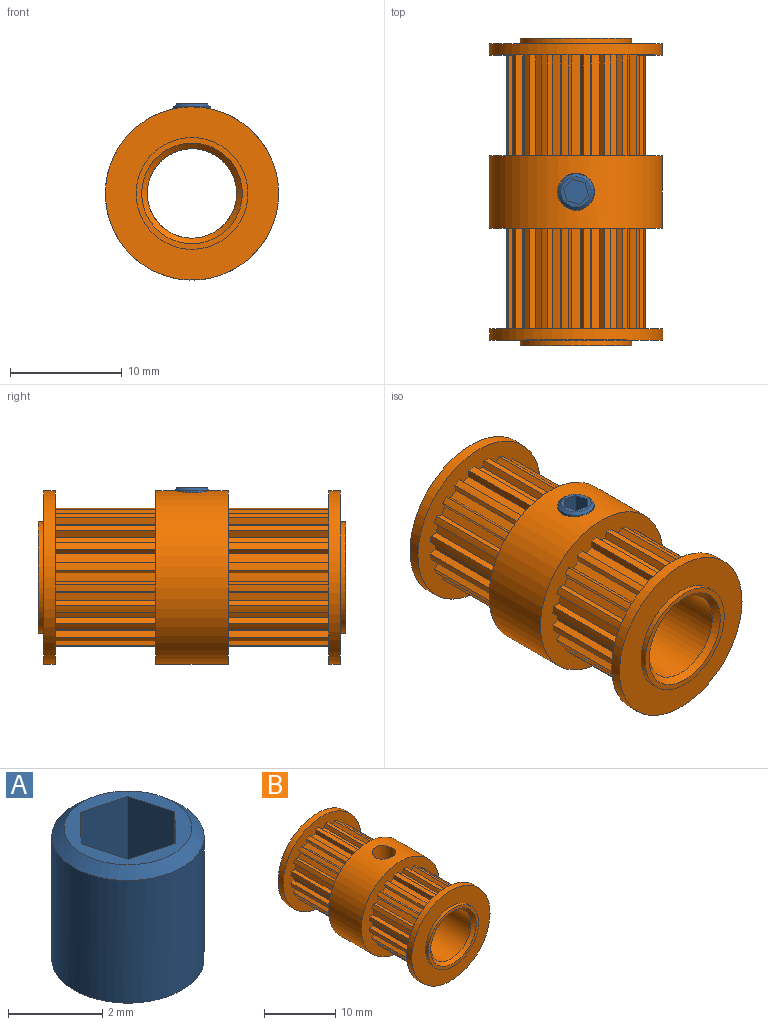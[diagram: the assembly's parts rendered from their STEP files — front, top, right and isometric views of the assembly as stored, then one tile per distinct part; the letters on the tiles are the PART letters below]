
ASSEMBLY  parts=2 mates=1
PART A: 12 faces, bbox 3.2x3.2x4 mm
  f0: plane 3x1.12mm, normal (0.25,0.97,0), area 3.5mm2, adj f1,f2,f4,f7
  f1: plane 3x1.11mm, normal (0.96,0.27,0), area 3.5mm2, adj f0,f3,f4,f7
  f2: plane 3x0.83mm, normal (-0.72,0.7,0), area 3.5mm2, adj f0,f4,f5,f7
  f3: plane 3x0.83mm, normal (0.72,-0.7,0), area 3.5mm2, adj f1,f4,f6,f7
  f4: plane 2.24x2.22mm, normal (0,0,1), area 3.5mm2, adj f0,f1,f2,f3,f5,f6
  f5: plane 3x1.11mm, normal (-0.96,-0.27,0), area 3.5mm2, adj f2,f4,f6,f7
  f6: plane 3x1.12mm, normal (-0.25,-0.97,0), area 3.5mm2, adj f3,f4,f5,f7
  f7: plane 2.71x2.71mm, normal (0,0,1), area 2.3mm2, adj f0,f1,f2,f3,f5,f6,f9
  f8: plane 1.19x1.19mm, normal (0,0,-1), area 1.1mm2, adj f10
  f9: cone r=1.61mm half-angle=48.9deg, axis (0,0,-1), area 3.2mm2, adj f7,f11
  f10: cone r=1.61mm half-angle=59.8deg, axis (0,0,1), area 8.2mm2, adj f8,f11
  f11: cylinder r=1.61mm len=3.23mm, axis (0,0,-1), area 32.3mm2, adj f9,f10
PART B: 177 faces, bbox 15.5x27.5x15.5 mm
  f0: plane 9x0.64mm, normal (1,0,-0.08), area 5.8mm2, adj f2,f3,f155,f167
  f1: plane 9x0.76mm, normal (0.95,0,0.31), area 7.2mm2, adj f4,f5,f158,f168
  f2: plane 9x0.76mm, normal (0.31,0,-0.95), area 7.2mm2, adj f0,f6,f155,f167
  f3: cylinder r=6.21mm len=9mm, axis (0,1,0), area 5.9mm2, adj f0,f7,f155,f167
  f4: plane 9x0.64mm, normal (0.08,0,1), area 5.8mm2, adj f1,f8,f158,f168
  f5: plane 9x0.49mm, normal (0.65,0,-0.76), area 5.8mm2, adj f1,f9,f158,f168
  f6: plane 9x0.49mm, normal (-0.76,0,-0.65), area 5.8mm2, adj f2,f10,f155,f167
  f7: plane 9x0.59mm, normal (-0.92,0,-0.38), area 5.8mm2, adj f3,f11,f155,f167
  f8: cylinder r=6.21mm len=9mm, axis (0,-1,0), area 5.9mm2, adj f4,f12,f158,f168
  f9: cylinder r=6.21mm len=9mm, axis (0,-1,0), area 5.9mm2, adj f5,f13,f158,f168
  f10: cylinder r=6.21mm len=9mm, axis (0,1,0), area 5.9mm2, adj f6,f14,f155,f167
  f11: plane 9x0.8mm, normal (0,0,-1), area 7.2mm2, adj f7,f15,f155,f167
  f12: plane 9x0.59mm, normal (0.38,0,-0.92), area 5.8mm2, adj f8,f16,f158,f168
  f13: plane 9x0.63mm, normal (-0.23,0,0.97), area 5.8mm2, adj f9,f17,f158,f168
  f14: plane 9x0.63mm, normal (0.97,0,0.23), area 5.8mm2, adj f10,f18,f155,f167
  f15: plane 9x0.59mm, normal (0.92,0,-0.38), area 5.8mm2, adj f11,f19,f155,f167
  f16: plane 9x0.8mm, normal (1,0,0), area 7.2mm2, adj f12,f20,f158,f168
  f17: plane 9x0.65mm, normal (0.81,0,0.59), area 7.2mm2, adj f13,f21,f158,f168
  f18: plane 9x0.65mm, normal (0.59,0,-0.81), area 7.2mm2, adj f14,f22,f155,f167
  f19: cylinder r=6.21mm len=9mm, axis (0,1,0), area 5.9mm2, adj f15,f23,f155,f167
  f20: plane 9x0.59mm, normal (0.38,0,0.92), area 5.8mm2, adj f16,f24,f158,f168
  f21: plane 9x0.55mm, normal (0.85,0,-0.52), area 5.8mm2, adj f17,f25,f158,f168
  f22: plane 9x0.55mm, normal (-0.52,0,-0.85), area 5.8mm2, adj f18,f26,f155,f167
  f23: plane 9x0.64mm, normal (-1,0,-0.08), area 5.8mm2, adj f19,f27,f155,f167
  f24: cylinder r=6.21mm len=9mm, axis (0,-1,0), area 5.9mm2, adj f20,f28,f158,f168
  f25: cylinder r=6.21mm len=9mm, axis (0,-1,0), area 5.9mm2, adj f21,f29,f158,f168
  f26: cylinder r=6.21mm len=9mm, axis (0,1,0), area 5.9mm2, adj f22,f30,f155,f167
  f27: plane 9x0.76mm, normal (-0.31,0,-0.95), area 7.2mm2, adj f23,f31,f155,f167
  f28: plane 9x0.64mm, normal (0.08,0,-1), area 5.8mm2, adj f24,f32,f158,f168
  f29: plane 9x0.55mm, normal (-0.52,0,0.85), area 5.8mm2, adj f25,f33,f158,f168
  f30: plane 9x0.55mm, normal (0.85,0,0.52), area 5.8mm2, adj f26,f34,f155,f167
  f31: plane 9x0.49mm, normal (0.76,0,-0.65), area 5.8mm2, adj f27,f35,f155,f167
  f32: plane 9x0.76mm, normal (0.95,0,-0.31), area 7.2mm2, adj f28,f36,f158,f168
  f33: plane 9x0.65mm, normal (0.59,0,0.81), area 7.2mm2, adj f29,f37,f158,f168
  f34: plane 9x0.65mm, normal (0.81,0,-0.59), area 7.2mm2, adj f30,f38,f155,f167
  f35: cylinder r=6.21mm len=9mm, axis (0,1,0), area 5.9mm2, adj f31,f39,f155,f167
  f36: plane 9x0.49mm, normal (0.65,0,0.76), area 5.8mm2, adj f32,f40,f158,f168
  f37: plane 9x0.63mm, normal (0.97,0,-0.23), area 5.8mm2, adj f33,f41,f158,f168
  f38: plane 9x0.63mm, normal (-0.23,0,-0.97), area 5.8mm2, adj f34,f42,f155,f167
  f39: plane 9x0.63mm, normal (-0.97,0,0.23), area 5.8mm2, adj f35,f43,f155,f167
  f40: cylinder r=6.21mm len=9mm, axis (0,-1,0), area 5.9mm2, adj f36,f44,f158,f168
  f41: cylinder r=6.21mm len=9mm, axis (0,-1,0), area 5.9mm2, adj f37,f45,f158,f168
  f42: cylinder r=6.21mm len=9mm, axis (0,1,0), area 5.9mm2, adj f38,f46,f155,f167
  f43: plane 9x0.65mm, normal (-0.59,0,-0.81), area 7.2mm2, adj f39,f47,f155,f167
  f44: plane 9x0.63mm, normal (-0.23,0,-0.97), area 5.8mm2, adj f40,f48,f158,f168
  f45: plane 9x0.49mm, normal (-0.76,0,0.65), area 5.8mm2, adj f41,f49,f158,f168
  f46: plane 9x0.49mm, normal (0.65,0,0.76), area 5.8mm2, adj f42,f50,f155,f167
  f47: plane 9x0.55mm, normal (0.52,0,-0.85), area 5.8mm2, adj f43,f51,f155,f167
  f48: plane 9x0.65mm, normal (0.81,0,-0.59), area 7.2mm2, adj f44,f52,f158,f168
  f49: plane 9x0.76mm, normal (0.31,0,0.95), area 7.2mm2, adj f45,f53,f158,f168
  f50: plane 9x0.76mm, normal (0.95,0,-0.31), area 7.2mm2, adj f46,f54,f155,f167
  f51: cylinder r=6.21mm len=9mm, axis (0,1,0), area 5.9mm2, adj f47,f55,f155,f167
  f52: plane 9x0.55mm, normal (0.85,0,0.52), area 5.8mm2, adj f48,f56,f158,f168
  f53: plane 9x0.64mm, normal (1,0,0.08), area 5.8mm2, adj f49,f57,f158,f168
  f54: plane 9x0.64mm, normal (0.08,0,-1), area 5.8mm2, adj f50,f58,f155,f167
  f55: plane 9x0.55mm, normal (-0.85,0,0.52), area 5.8mm2, adj f51,f59,f155,f167
  f56: cylinder r=6.21mm len=9mm, axis (0,-1,0), area 5.9mm2, adj f52,f60,f158,f168
  f57: cylinder r=6.21mm len=9mm, axis (0,-1,0), area 5.9mm2, adj f53,f61,f158,f168
  f58: cylinder r=6.21mm len=9mm, axis (0,1,0), area 5.9mm2, adj f54,f62,f155,f167
  f59: plane 9x0.65mm, normal (-0.81,0,-0.59), area 7.2mm2, adj f55,f63,f155,f167
  f60: plane 9x0.55mm, normal (-0.52,0,-0.85), area 5.8mm2, adj f56,f64,f158,f168
  f61: plane 9x0.59mm, normal (-0.92,0,0.38), area 5.8mm2, adj f57,f65,f158,f168
  f62: plane 9x0.59mm, normal (0.38,0,0.92), area 5.8mm2, adj f58,f66,f155,f167
  f63: plane 9x0.63mm, normal (0.23,0,-0.97), area 5.8mm2, adj f59,f67,f155,f167
  f64: plane 9x0.65mm, normal (0.59,0,-0.81), area 7.2mm2, adj f60,f68,f158,f168
  f65: plane 9x0.8mm, normal (0,0,1), area 7.2mm2, adj f61,f69,f158,f168
  f66: plane 9x0.8mm, normal (1,0,0), area 7.2mm2, adj f62,f70,f155,f167
  f67: cylinder r=6.21mm len=9mm, axis (0,1,0), area 5.9mm2, adj f63,f71,f155,f167
  f68: plane 9x0.63mm, normal (0.97,0,0.23), area 5.8mm2, adj f64,f72,f158,f168
  f69: plane 9x0.59mm, normal (0.92,0,0.38), area 5.8mm2, adj f65,f73,f158,f168
  f70: plane 9x0.59mm, normal (0.38,0,-0.92), area 5.8mm2, adj f66,f74,f155,f167
  f71: plane 9x0.49mm, normal (-0.65,0,0.76), area 5.8mm2, adj f67,f75,f155,f167
  f72: cylinder r=6.21mm len=9mm, axis (0,-1,0), area 5.9mm2, adj f68,f76,f158,f168
  f73: cylinder r=6.21mm len=9mm, axis (0,-1,0), area 5.9mm2, adj f69,f77,f158,f168
  f74: cylinder r=6.21mm len=9mm, axis (0,1,0), area 5.9mm2, adj f70,f78,f155,f167
  f75: plane 9x0.76mm, normal (-0.95,0,-0.31), area 7.2mm2, adj f71,f79,f155,f167
  f76: plane 9x0.49mm, normal (-0.76,0,-0.65), area 5.8mm2, adj f72,f80,f158,f168
  f77: plane 9x0.64mm, normal (-1,0,0.08), area 5.8mm2, adj f73,f81,f158,f168
  f78: plane 9x0.64mm, normal (0.08,0,1), area 5.8mm2, adj f74,f82,f155,f167
  f79: plane 9x0.64mm, normal (-0.08,0,-1), area 5.8mm2, adj f75,f83,f155,f167
  f80: plane 9x0.76mm, normal (0.31,0,-0.95), area 7.2mm2, adj f76,f84,f158,f168
  f81: plane 9x0.76mm, normal (-0.31,0,0.95), area 7.2mm2, adj f77,f85,f158,f168
  f82: plane 9x0.76mm, normal (0.95,0,0.31), area 7.2mm2, adj f78,f86,f155,f167
  f83: cylinder r=6.21mm len=9mm, axis (0,1,0), area 5.9mm2, adj f79,f87,f155,f167
  f84: plane 9x0.64mm, normal (1,0,-0.08), area 5.8mm2, adj f80,f88,f158,f168
  f85: plane 9x0.49mm, normal (0.76,0,0.65), area 5.8mm2, adj f81,f89,f158,f168
  f86: plane 9x0.49mm, normal (0.65,0,-0.76), area 5.8mm2, adj f82,f90,f155,f167
  f87: plane 9x0.59mm, normal (-0.38,0,0.92), area 5.8mm2, adj f83,f91,f155,f167
  f88: cylinder r=6.21mm len=9mm, axis (0,-1,0), area 5.9mm2, adj f84,f92,f158,f168
  f89: cylinder r=6.21mm len=9mm, axis (0,-1,0), area 5.9mm2, adj f85,f93,f158,f168
  f90: cylinder r=6.21mm len=9mm, axis (0,1,0), area 5.9mm2, adj f86,f94,f155,f167
  f91: plane 9x0.8mm, normal (-1,0,0), area 7.2mm2, adj f87,f95,f155,f167
  f92: plane 9x0.59mm, normal (-0.92,0,-0.38), area 5.8mm2, adj f88,f96,f158,f168
  f93: plane 9x0.63mm, normal (-0.97,0,-0.23), area 5.8mm2, adj f89,f97,f158,f168
  f94: plane 9x0.63mm, normal (-0.23,0,0.97), area 5.8mm2, adj f90,f98,f155,f167
  f95: plane 9x0.59mm, normal (-0.38,0,-0.92), area 5.8mm2, adj f91,f99,f155,f167
  f96: plane 9x0.8mm, normal (0,0,-1), area 7.2mm2, adj f92,f100,f158,f168
  f97: plane 9x0.65mm, normal (-0.59,0,0.81), area 7.2mm2, adj f93,f101,f158,f168
  f98: plane 9x0.65mm, normal (0.81,0,0.59), area 7.2mm2, adj f94,f102,f155,f167
  f99: cylinder r=6.21mm len=9mm, axis (0,1,0), area 5.9mm2, adj f95,f103,f155,f167
  f100: plane 9x0.59mm, normal (0.92,0,-0.38), area 5.8mm2, adj f96,f104,f158,f168
  f101: plane 9x0.55mm, normal (0.52,0,0.85), area 5.8mm2, adj f97,f105,f158,f168
  f102: plane 9x0.55mm, normal (0.85,0,-0.52), area 5.8mm2, adj f98,f106,f155,f167
  f103: plane 9x0.64mm, normal (-0.08,0,1), area 5.8mm2, adj f99,f107,f155,f167
  f104: cylinder r=6.21mm len=9mm, axis (0,-1,0), area 5.9mm2, adj f100,f108,f158,f168
  f105: cylinder r=6.21mm len=9mm, axis (0,-1,0), area 5.9mm2, adj f101,f109,f158,f168
  f106: cylinder r=6.21mm len=9mm, axis (0,1,0), area 5.9mm2, adj f102,f110,f155,f167
  f107: plane 9x0.76mm, normal (-0.95,0,0.31), area 7.2mm2, adj f103,f111,f155,f167
  f108: plane 9x0.64mm, normal (-1,0,-0.08), area 5.8mm2, adj f104,f112,f158,f168
  f109: plane 9x0.55mm, normal (-0.85,0,-0.52), area 5.8mm2, adj f105,f113,f158,f168
  f110: plane 9x0.55mm, normal (-0.52,0,0.85), area 5.8mm2, adj f106,f114,f155,f167
  f111: plane 9x0.49mm, normal (-0.65,0,-0.76), area 5.8mm2, adj f107,f115,f155,f167
  f112: plane 9x0.76mm, normal (-0.31,0,-0.95), area 7.2mm2, adj f108,f116,f158,f168
  f113: plane 9x0.65mm, normal (-0.81,0,0.59), area 7.2mm2, adj f109,f117,f158,f168
  f114: plane 9x0.65mm, normal (0.59,0,0.81), area 7.2mm2, adj f110,f118,f155,f167
  f115: cylinder r=6.21mm len=9mm, axis (0,1,0), area 5.9mm2, adj f111,f119,f155,f167
  f116: plane 9x0.49mm, normal (0.76,0,-0.65), area 5.8mm2, adj f112,f120,f158,f168
  f117: plane 9x0.63mm, normal (0.23,0,0.97), area 5.8mm2, adj f113,f121,f158,f168
  f118: plane 9x0.63mm, normal (0.97,0,-0.23), area 5.8mm2, adj f114,f122,f155,f167
  f119: plane 9x0.63mm, normal (0.23,0,0.97), area 5.8mm2, adj f115,f123,f155,f167
  f120: cylinder r=6.21mm len=9mm, axis (0,-1,0), area 5.9mm2, adj f116,f124,f158,f168
  f121: cylinder r=6.21mm len=9mm, axis (0,-1,0), area 5.9mm2, adj f117,f125,f158,f168
  f122: cylinder r=6.21mm len=9mm, axis (0,1,0), area 5.9mm2, adj f118,f126,f155,f167
  f123: plane 9x0.65mm, normal (-0.81,0,0.59), area 7.2mm2, adj f119,f127,f155,f167
  f124: plane 9x0.63mm, normal (-0.97,0,0.23), area 5.8mm2, adj f120,f128,f158,f168
  f125: plane 9x0.49mm, normal (-0.65,0,-0.76), area 5.8mm2, adj f121,f129,f158,f168
  f126: plane 9x0.49mm, normal (-0.76,0,0.65), area 5.8mm2, adj f122,f130,f155,f167
  f127: plane 9x0.55mm, normal (-0.85,0,-0.52), area 5.8mm2, adj f123,f131,f155,f167
  f128: plane 9x0.65mm, normal (-0.59,0,-0.81), area 7.2mm2, adj f124,f132,f158,f168
  f129: plane 9x0.76mm, normal (-0.95,0,0.31), area 7.2mm2, adj f125,f133,f158,f168
  f130: plane 9x0.76mm, normal (0.31,0,0.95), area 7.2mm2, adj f126,f134,f155,f167
  f131: cylinder r=6.21mm len=9mm, axis (0,1,0), area 5.9mm2, adj f127,f135,f155,f167
  f132: plane 9x0.55mm, normal (0.52,0,-0.85), area 5.8mm2, adj f128,f136,f158,f168
  f133: plane 9x0.64mm, normal (-0.08,0,1), area 5.8mm2, adj f129,f137,f158,f168
  f134: plane 9x0.64mm, normal (1,0,0.08), area 5.8mm2, adj f130,f138,f155,f167
  f135: plane 9x0.55mm, normal (0.52,0,0.85), area 5.8mm2, adj f131,f139,f155,f167
  f136: cylinder r=6.21mm len=9mm, axis (0,-1,0), area 5.9mm2, adj f132,f140,f158,f168
  f137: cylinder r=6.21mm len=9mm, axis (0,-1,0), area 5.9mm2, adj f133,f141,f158,f168
  f138: cylinder r=6.21mm len=9mm, axis (0,1,0), area 5.9mm2, adj f134,f142,f155,f167
  f139: plane 9x0.65mm, normal (-0.59,0,0.81), area 7.2mm2, adj f135,f143,f155,f167
  f140: plane 9x0.55mm, normal (-0.85,0,0.52), area 5.8mm2, adj f136,f144,f158,f168
  f141: plane 9x0.59mm, normal (-0.38,0,-0.92), area 5.8mm2, adj f137,f145,f158,f168
  f142: plane 9x0.59mm, normal (-0.92,0,0.38), area 5.8mm2, adj f138,f146,f155,f167
  f143: plane 9x0.63mm, normal (-0.97,0,-0.23), area 5.8mm2, adj f139,f147,f155,f167
  f144: plane 9x0.65mm, normal (-0.81,0,-0.59), area 7.2mm2, adj f140,f148,f158,f168
  f145: plane 9x0.8mm, normal (-1,0,0), area 7.2mm2, adj f141,f149,f158,f168
  f146: plane 9x0.8mm, normal (0,0,1), area 7.2mm2, adj f142,f150,f155,f167
  f147: cylinder r=6.21mm len=9mm, axis (0,1,0), area 5.9mm2, adj f143,f151,f155,f167
  f148: plane 9x0.63mm, normal (0.23,0,-0.97), area 5.8mm2, adj f144,f152,f158,f168
  f149: plane 9x0.59mm, normal (-0.38,0,0.92), area 5.8mm2, adj f145,f153,f158,f168
  f150: plane 9x0.59mm, normal (0.92,0,0.38), area 5.8mm2, adj f146,f155,f156,f167
  f151: plane 9x0.49mm, normal (0.76,0,0.65), area 5.8mm2, adj f147,f155,f157,f167
  f152: cylinder r=6.21mm len=9mm, axis (0,-1,0), area 5.9mm2, adj f148,f158,f159,f168
  f153: cylinder r=6.21mm len=9mm, axis (0,-1,0), area 5.9mm2, adj f149,f158,f160,f168
  f154: cylinder r=7.75mm len=15.5mm, axis (0,1,0), area 48.7mm2, adj f158,f162
  f155: plane 15.5x15.5mm, normal (0,1,0), area 80.4mm2, adj f0,f2,f3,f6,f7,f10,f11,f14
  f156: cylinder r=6.21mm len=9mm, axis (0,1,0), area 5.9mm2, adj f150,f155,f163,f167
  f157: plane 9x0.76mm, normal (-0.31,0,0.95), area 7.2mm2, adj f151,f155,f163,f167
  f158: plane 15.5x15.5mm, normal (0,-1,0), area 80.4mm2, adj f1,f4,f5,f8,f9,f12,f13,f16
  f159: plane 9x0.49mm, normal (-0.65,0,0.76), area 5.8mm2, adj f152,f158,f164,f168
  f160: plane 9x0.64mm, normal (-0.08,0,-1), area 5.8mm2, adj f153,f158,f164,f168
  f161: cylinder r=7.75mm len=15.5mm, axis (0,-1,0), area 48.7mm2, adj f155,f165
  f162: plane 15.5x15.5mm, normal (0,1,0), area 110.2mm2, adj f154,f166
  f163: plane 9x0.64mm, normal (-1,0,0.08), area 5.8mm2, adj f155,f156,f157,f167
  f164: plane 9x0.76mm, normal (-0.95,0,-0.31), area 7.2mm2, adj f158,f159,f160,f168
  f165: plane 15.5x15.5mm, normal (0,-1,0), area 110.2mm2, adj f161,f169
  f166: cylinder r=5mm len=10mm, axis (0,-1,0), area 15.7mm2, adj f162,f170
  f167: plane 15.5x15.5mm, normal (0,-1,0), area 80.4mm2, adj f0,f2,f3,f6,f7,f10,f11,f14
  f168: plane 15.5x15.5mm, normal (0,1,0), area 80.4mm2, adj f1,f4,f5,f8,f9,f12,f13,f16
  f169: cylinder r=5mm len=10mm, axis (0,1,0), area 15.7mm2, adj f165,f172
  f170: plane 10x10mm, normal (0,1,0), area 14.9mm2, adj f166,f173
  f171: cylinder r=7.75mm len=15.5mm, axis (0,1,0), area 307.9mm2, adj f167,f168,f174
  f172: plane 10x10mm, normal (0,-1,0), area 14.9mm2, adj f169,f175
  f173: cone r=4.5mm half-angle=45deg, axis (0,1,0), area 18.9mm2, adj f170,f176
  f174: cylinder r=1.65mm len=4.11mm, axis (0,0,-1), area 39.8mm2, adj f171,f176
  f175: cone r=4.5mm half-angle=45deg, axis (0,-1,0), area 18.9mm2, adj f172,f176
  f176: cylinder r=4mm len=26.5mm, axis (0,-1,0), area 657.3mm2, adj f173,f174,f175
PLACE A t=(0,0,-1)mm
PLACE B at identity
MATE fastened A.f9 <-> B.f174  axis (0,0,-1) through (0,-3.25,7.78)mm
